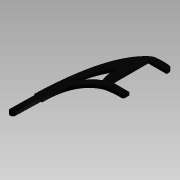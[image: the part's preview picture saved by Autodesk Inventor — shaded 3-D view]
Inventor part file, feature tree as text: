
AUTODESK INVENTOR PART (.ipt)
format: ipt  version: 2015 SP1 (Build 190203100, 203)  size: 184,832 bytes
history: native  units: mm
features: fillet x4, extrude x2, sketch x1
ambient origin geometry x8: Origin, YZ Plane, XZ Plane, XY Plane, X Axis, Y Axis, Z Axis, Center Point
bodies: Solid1 (feature_tree)
feature tree (7):
  sketch  "Sketch1"  dims[d2=6.0mm d3=20.45mm d4=21.0mm d5=2.2352mm d6=5.16mm d7=3.64mm d8=42.0mm d9=3.3mm d11=42.0mm d12=8.67mm d17=1.3mm d18=1.3mm d19=6.7mm d20=2.0mm d21=2.2352mm d22=9.8044mm d23=2.2352mm d24=2.2352mm d25=9.8044mm d26=49.1998mm d27=3.5mm d28=0.0mm d29=9.0mm d30=4.0mm d31=0.25mm d34=131.9mm d35=3.285mm d36=10.0mm d37=0.0mm d38=1.0mm]
  extrude  "Extrusion1"  Depth=20.45mm
  fillet  "Fillet1"  Radius=21.0mm
  fillet  "Fillet2"  Radius=2.2352mm
  fillet  "Fillet3"  Radius=5.16mm
  extrude  "Extrusion2"  Depth=3.64mm
  fillet  "Fillet5"  Radius=42.0mm
